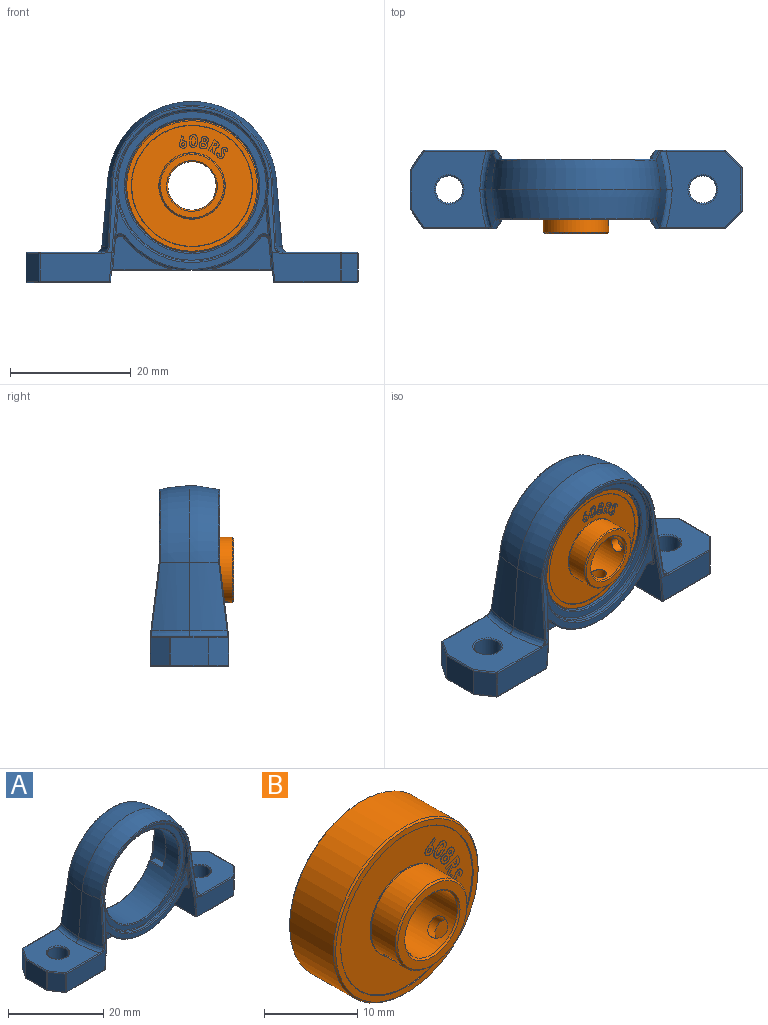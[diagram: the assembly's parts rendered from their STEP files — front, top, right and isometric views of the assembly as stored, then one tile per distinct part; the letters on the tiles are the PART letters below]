
ASSEMBLY  parts=2 mates=1
PART A: 247 faces, bbox 55.2x14x30.2 mm
  f0: plane 22.96x7.55mm, normal (0,1,0), area 35.1mm2, adj f36,f150,f153,f155
  f1: plane 13.6x12.6mm, normal (0,0,-1), area 145.8mm2, adj f133,f134,f135,f136,f137,f138,f139
  f2: plane 12.6x12.38mm, normal (0,0,1), area 122.3mm2, adj f57,f58,f118,f119,f120,f121,f122,f147
  f3: plane 11.31x4.79mm, normal (0,1,0), area 51.3mm2, adj f124,f125,f145,f196,f202,f233
  f4: plane 11.9x4.79mm, normal (0,1,0), area 54mm2, adj f117,f118,f135,f195,f199,f230
  f5: plane 13.6x12.6mm, normal (0,0,-1), area 145.2mm2, adj f140,f141,f142,f143,f144,f145,f146
  f6: plane 7.18x4.6mm, normal (1,0,0), area 33mm2, adj f127,f141,f236,f239
  f7: plane 12.6x12.38mm, normal (0,0,1), area 121.7mm2, adj f55,f56,f125,f126,f127,f128,f129,f148
  f8: plane 6.22x4.6mm, normal (-1,0,0), area 28.6mm2, adj f120,f138,f224,f227
  f9: plane 26.19x11.92mm, normal (0,1,0), area 17mm2, adj f209,f217,f218,f222
  f10: plane 12.19x1.74mm, normal (0,0.99,0.12), area 7.6mm2, adj f199,f200,f207,f208,f212,f217
  f11: plane 12.19x1.74mm, normal (0,0.99,0.12), area 7.6mm2, adj f201,f202,f210,f211,f215,f218,f219
  f12: cylinder r=14mm len=22.23mm, axis (0,-1,0), area 92.4mm2, adj f51,f53,f64,f65,f69,f70,f107
  f13: plane 13.76x12.77mm, normal (-1,0,-0.09), area 79.2mm2, adj f51,f52,f74,f78,f80,f81,f84,f94
  f14: plane 13.76x12.77mm, normal (1,0,-0.09), area 79.2mm2, adj f53,f54,f77,f79,f82,f85,f89,f100
  f15: plane 25.25x10.33mm, normal (0,1,0), area 37.6mm2, adj f105,f107,f109,f110,f113,f114
  f16: cylinder r=11mm len=22mm, axis (0,1,0), area 448.7mm2, adj f47,f50,f132,f149,f152,f153,f157,f160
  f17: plane 26.19x11.92mm, normal (0,-1,0), area 17mm2, adj f179,f187,f188,f192
  f18: plane 11.31x4.79mm, normal (0,-1,0), area 51.3mm2, adj f129,f130,f144,f165,f169,f242
  f19: plane 11.9x4.79mm, normal (0,-1,0), area 54mm2, adj f122,f123,f134,f166,f172,f245
  f20: plane 12.19x1.74mm, normal (0,-0.99,0.12), area 7.6mm2, adj f171,f172,f180,f181,f185,f188
  f21: plane 12.19x1.74mm, normal (0,-0.99,0.12), area 7.6mm2, adj f169,f170,f177,f178,f182,f186,f187
  f22: cylinder r=14mm len=22.23mm, axis (0,1,0), area 92.4mm2, adj f52,f54,f62,f63,f86,f92,f95
  f23: plane 25.25x10.33mm, normal (0,-1,0), area 37.6mm2, adj f93,f95,f97,f98,f101,f102
  f24: cylinder r=12.5mm len=25mm, axis (0,-1,0), area 48.8mm2, adj f96,f99,f101,f103,f104,f131,f178,f179
  f25: plane 24.6x24.6mm, normal (0,-1,0), area 81.2mm2, adj f131,f132
  f26: plane 26.31x1.6mm, normal (0,0,-1), area 42.1mm2, adj f59,f60,f67,f68,f75,f76,f81,f82
  f27: plane 9.77x5.48mm, normal (0,-1,0), area 24mm2, adj f88,f89,f91,f92
  f28: plane 9.77x5.48mm, normal (0,-1,0), area 24mm2, adj f80,f83,f86,f87
  f29: cylinder r=25.08mm len=11.46mm, axis (-0.09,0,-1), area 63.8mm2, adj f31,f40,f57,f185,f189
  f30: cylinder r=25.08mm len=11.4mm, axis (-0.09,0,1), area 63.5mm2, adj f31,f41,f55,f182
  f31: revolved ~27.89x12.9mm, area 199.8mm2, adj f29,f30,f42,f186,f190,f191,f192
  f32: cylinder r=2.25mm len=4.6mm, axis (0,0,1), area 65mm2, adj f139,f147
  f33: plane 4.6x3.19mm, normal (-0.83,-0.55,0), area 17.6mm2, adj f121,f136,f224,f245
  f34: plane 4.6x2.71mm, normal (0.71,-0.71,0), area 17.6mm2, adj f128,f142,f239,f242
  f35: cylinder r=2.25mm len=4.6mm, axis (0,0,1), area 65mm2, adj f140,f148
  f36: cylinder r=12.5mm len=25mm, axis (0,1,0), area 142.5mm2, adj f0,f37,f45,f46,f47,f48,f49,f50
  f37: plane 22.96x7.55mm, normal (0,1,0), area 35.1mm2, adj f36,f156,f159,f160
  f38: plane 9.77x5.48mm, normal (0,1,0), area 24mm2, adj f70,f73,f76,f77
  f39: plane 9.77x5.48mm, normal (0,1,0), area 24mm2, adj f69,f71,f74,f75
  f40: cylinder r=25.09mm len=11.46mm, axis (-0.09,0,-1), area 63.8mm2, adj f29,f42,f58,f212,f216
  f41: cylinder r=25.09mm len=11.4mm, axis (-0.09,0,1), area 63.5mm2, adj f30,f42,f56,f215
  f42: revolved ~27.89x12.9mm, area 199.8mm2, adj f31,f40,f41,f219,f220,f221,f222
  f43: plane 4.6x3.19mm, normal (-0.83,0.55,0), area 17.6mm2, adj f119,f137,f227,f230
  f44: plane 4.6x2.71mm, normal (0.71,0.71,0), area 17.6mm2, adj f126,f143,f233,f236
  f45: plane 3.8x1.52mm, normal (0,0,-1), area 5.8mm2, adj f36,f47,f152,f155
  f46: plane 3.8x1.52mm, normal (0,0,1), area 5.8mm2, adj f36,f47,f159,f162
  f47: plane 9.72x2.63mm, normal (0,1,0), area 14.7mm2, adj f16,f36,f45,f46,f152,f162
  f48: plane 3.8x1.52mm, normal (0,0,-1), area 5.8mm2, adj f36,f50,f149,f150
  f49: plane 3.8x1.52mm, normal (0,0,1), area 5.8mm2, adj f36,f50,f156,f157
  f50: plane 9.72x2.63mm, normal (0,1,0), area 14.7mm2, adj f16,f36,f48,f49,f149,f157
  f51: cylinder r=1mm len=3.6mm, axis (0,-1,0), area 8.6mm2, adj f12,f13,f71,f110
  f52: cylinder r=1mm len=3.6mm, axis (0,1,0), area 8.6mm2, adj f13,f22,f83,f93
  f53: cylinder r=1mm len=3.6mm, axis (0,-1,0), area 8.6mm2, adj f12,f14,f73,f105
  f54: cylinder r=1mm len=3.6mm, axis (0,1,0), area 8.6mm2, adj f14,f22,f91,f98
  f55: bspline ~11.42x2.29mm, area 9.5mm2, adj f7,f30,f56,f130,f177
  f56: bspline ~7.28x2.2mm, area 9.5mm2, adj f7,f41,f55,f124,f211
  f57: bspline ~11.42x2.29mm, area 9.5mm2, adj f2,f29,f58,f123,f181
  f58: bspline ~8.05x2.18mm, area 9.5mm2, adj f2,f40,f57,f117,f207
  f59: bspline ~3.35x0.2mm, area 0.6mm2, adj f26,f60,f88,f90
  f60: bspline ~3.35x0.2mm, area 0.6mm2, adj f26,f59,f61,f87
  f61: bspline ~3.35x0.34mm, area 0.4mm2, adj f60,f62,f86,f87
  f62: bspline ~3.31x0.39mm, area 0.5mm2, adj f22,f61,f63,f86
  f63: bspline ~3.31x0.39mm, area 0.5mm2, adj f22,f62,f90,f92
  f64: bspline ~3.31x0.39mm, area 0.5mm2, adj f12,f65,f70,f72
  f65: bspline ~3.31x0.39mm, area 0.5mm2, adj f12,f64,f66,f69
  f66: bspline ~3.35x0.34mm, area 0.4mm2, adj f65,f67,f69,f75
  f67: bspline ~3.35x0.2mm, area 0.6mm2, adj f26,f66,f68,f75
  f68: bspline ~3.35x0.2mm, area 0.6mm2, adj f26,f67,f72,f76
  f69: torus R=14.2mm, axis (0,-1,0), area 3mm2, adj f12,f39,f65,f66,f71
  f70: torus R=14.2mm, axis (0,-1,0), area 3mm2, adj f12,f38,f64,f72,f73
  f71: torus R=0.8mm, axis (0,-1,0), area 0.7mm2, adj f39,f51,f69,f74
  f72: bspline ~3.35x0.34mm, area 0.4mm2, adj f64,f68,f70,f76
  f73: torus R=0.8mm, axis (0,-1,0), area 0.7mm2, adj f38,f53,f70,f77
  f74: cylinder r=0.2mm len=4.76mm, axis (0.09,0,-1), area 1.5mm2, adj f13,f39,f71,f78
  f75: cylinder r=0.2mm len=9.81mm, axis (1,0,0), area 3.1mm2, adj f26,f39,f66,f67,f78
  f76: cylinder r=0.2mm len=9.81mm, axis (1,0,0), area 3.1mm2, adj f26,f38,f68,f72,f79
  f77: cylinder r=0.2mm len=4.76mm, axis (-0.09,0,-1), area 1.5mm2, adj f14,f38,f73,f79
  f78: bspline ~0.4x0.4mm, area 0.1mm2, adj f13,f74,f75,f81
  f79: bspline ~0.47x0.47mm, area 0.1mm2, adj f14,f76,f77,f82
  f80: cylinder r=0.2mm len=4.76mm, axis (0.09,0,-1), area 1.5mm2, adj f13,f28,f83,f84
  f81: cylinder r=0.2mm len=1.6mm, axis (0,1,0), area 0.5mm2, adj f13,f26,f78,f84
  f82: cylinder r=0.2mm len=1.6mm, axis (0,-1,0), area 0.5mm2, adj f14,f26,f79,f85
  f83: torus R=0.8mm, axis (0,1,0), area 0.7mm2, adj f28,f52,f80,f86
  f84: bspline ~0.5x0.4mm, area 0.1mm2, adj f13,f80,f81,f87
  f85: bspline ~0.47x0.42mm, area 0.1mm2, adj f14,f82,f88,f89
  f86: torus R=14.2mm, axis (0,1,0), area 3mm2, adj f22,f28,f61,f62,f83
  f87: cylinder r=0.2mm len=9.81mm, axis (1,0,0), area 3.1mm2, adj f26,f28,f60,f61,f84
  f88: cylinder r=0.2mm len=9.81mm, axis (1,0,0), area 3.1mm2, adj f26,f27,f59,f85,f90
  f89: cylinder r=0.2mm len=4.76mm, axis (-0.09,0,-1), area 1.5mm2, adj f14,f27,f85,f91
  f90: bspline ~3.35x0.34mm, area 0.4mm2, adj f59,f63,f88,f92
  f91: torus R=0.8mm, axis (0,1,0), area 0.7mm2, adj f27,f54,f89,f92
  f92: torus R=14.2mm, axis (0,1,0), area 3mm2, adj f22,f27,f63,f90,f91
  f93: torus R=1.2mm, axis (0,-1,0), area 0.7mm2, adj f23,f52,f94,f95
  f94: bspline ~1.03x0.4mm, area 0.1mm2, adj f13,f93,f97
  f95: torus R=13.8mm, axis (0,-1,0), area 8mm2, adj f22,f23,f93,f98
  f96: cylinder r=0.2mm len=0.05mm, axis (0,-1,0), area 0mm2, adj f13,f24,f99,f174
  f97: cylinder r=0.2mm len=5.94mm, axis (-0.09,0,1), area 1.7mm2, adj f13,f23,f94,f99
  f98: torus R=1.2mm, axis (0,-1,0), area 0.7mm2, adj f23,f54,f95,f100
  f99: bspline ~1.39x0.42mm, area 0.3mm2, adj f24,f96,f97,f101
  f100: bspline ~1.03x0.4mm, area 0.1mm2, adj f14,f98,f102
  f101: torus R=12.7mm, axis (0,-1,0), area 10.2mm2, adj f23,f24,f99,f103
  f102: cylinder r=0.2mm len=5.94mm, axis (-0.09,0,-1), area 1.7mm2, adj f14,f23,f100,f103
  f103: bspline ~1.39x0.43mm, area 0.3mm2, adj f24,f101,f102,f104
  f104: cylinder r=0.2mm len=0.05mm, axis (0,-1,0), area 0mm2, adj f14,f24,f103,f175
  f105: torus R=1.2mm, axis (0,1,0), area 0.7mm2, adj f15,f53,f106,f107
  f106: bspline ~1.03x0.4mm, area 0.1mm2, adj f14,f105,f109
  f107: torus R=13.8mm, axis (0,1,0), area 8mm2, adj f12,f15,f105,f110
  f108: cylinder r=0.2mm len=0.05mm, axis (0,1,0), area 0mm2, adj f14,f36,f111,f204
  f109: cylinder r=0.2mm len=5.94mm, axis (-0.09,0,-1), area 1.7mm2, adj f14,f15,f106,f111
  f110: torus R=1.2mm, axis (0,1,0), area 0.7mm2, adj f15,f51,f107,f112
  f111: bspline ~1.39x0.42mm, area 0.3mm2, adj f36,f108,f109,f113
  f112: bspline ~1.03x0.4mm, area 0.1mm2, adj f13,f110,f114
  f113: torus R=12.7mm, axis (0,1,0), area 10.2mm2, adj f15,f36,f111,f115
  f114: cylinder r=0.2mm len=5.94mm, axis (-0.09,0,1), area 1.7mm2, adj f13,f15,f112,f115
  f115: bspline ~1.39x0.43mm, area 0.3mm2, adj f36,f113,f114,f116
  f116: cylinder r=0.2mm len=0.05mm, axis (0,1,0), area 0mm2, adj f13,f36,f115,f205
  f117: bspline ~1.15x0.47mm, area 0.2mm2, adj f4,f58,f118,f203
  f118: cylinder r=0.2mm len=10.25mm, axis (-1,0,0), area 3.2mm2, adj f2,f4,f117,f229
  f119: cylinder r=0.2mm len=3.3mm, axis (0.55,0.83,0), area 1.2mm2, adj f2,f43,f226,f229
  f120: cylinder r=0.2mm len=6.22mm, axis (0,1,0), area 2mm2, adj f2,f8,f223,f226
  f121: cylinder r=0.2mm len=3.3mm, axis (-0.55,0.83,0), area 1.2mm2, adj f2,f33,f223,f244
  f122: cylinder r=0.2mm len=10.25mm, axis (-1,0,0), area 3.2mm2, adj f2,f19,f123,f244
  f123: bspline ~1.15x0.47mm, area 0.2mm2, adj f19,f57,f122,f176
  f124: bspline ~1.15x0.47mm, area 0.2mm2, adj f3,f56,f125,f206
  f125: cylinder r=0.2mm len=9.67mm, axis (-1,0,0), area 3mm2, adj f3,f7,f124,f232
  f126: cylinder r=0.2mm len=2.85mm, axis (-0.71,0.71,0), area 1.2mm2, adj f7,f44,f232,f235
  f127: cylinder r=0.2mm len=7.18mm, axis (0,1,0), area 2.3mm2, adj f6,f7,f235,f238
  f128: cylinder r=0.2mm len=2.85mm, axis (0.71,0.71,0), area 1.2mm2, adj f7,f34,f238,f241
  f129: cylinder r=0.2mm len=9.67mm, axis (-1,0,0), area 3mm2, adj f7,f18,f130,f241
  f130: bspline ~1.15x0.47mm, area 0.2mm2, adj f18,f55,f129,f173
  f131: torus R=12.3mm, axis (0,-1,0), area 24.5mm2, adj f24,f25
  f132: torus R=11.2mm, axis (0,-1,0), area 21.9mm2, adj f16,f25
  f133: cylinder r=0.2mm len=12.6mm, axis (0,-1,0), area 3.7mm2, adj f1,f14,f164,f193
  f134: cylinder r=0.2mm len=11.48mm, axis (1,0,0), area 3.6mm2, adj f1,f19,f164,f246
  f135: cylinder r=0.2mm len=11.48mm, axis (1,0,0), area 3.6mm2, adj f1,f4,f193,f231
  f136: cylinder r=0.2mm len=3.3mm, axis (-0.55,0.83,0), area 1.2mm2, adj f1,f33,f225,f246
  f137: cylinder r=0.2mm len=3.3mm, axis (0.55,0.83,0), area 1.2mm2, adj f1,f43,f228,f231
  f138: cylinder r=0.2mm len=6.22mm, axis (0,1,0), area 2mm2, adj f1,f8,f225,f228
  f139: torus R=2.45mm, axis (0,0,1), area 4.6mm2, adj f1,f32
  f140: torus R=2.45mm, axis (0,0,-1), area 4.6mm2, adj f5,f35
  f141: cylinder r=0.2mm len=7.18mm, axis (0,1,0), area 2.3mm2, adj f5,f6,f237,f240
  f142: cylinder r=0.2mm len=2.85mm, axis (0.71,0.71,0), area 1.2mm2, adj f5,f34,f240,f243
  f143: cylinder r=0.2mm len=2.85mm, axis (-0.71,0.71,0), area 1.2mm2, adj f5,f44,f234,f237
  f144: cylinder r=0.2mm len=10.89mm, axis (1,0,0), area 3.4mm2, adj f5,f18,f163,f243
  f145: cylinder r=0.2mm len=10.89mm, axis (1,0,0), area 3.4mm2, adj f3,f5,f194,f234
  f146: cylinder r=0.2mm len=12.6mm, axis (0,-1,0), area 3.7mm2, adj f5,f13,f163,f194
  f147: torus R=2.45mm, axis (0,0,-1), area 4.6mm2, adj f2,f32
  f148: torus R=2.45mm, axis (0,0,1), area 4.6mm2, adj f7,f35
  f149: cylinder r=0.2mm len=3.8mm, axis (0,1,0), area 0.8mm2, adj f16,f48,f50,f151
  f150: cylinder r=0.2mm len=1.52mm, axis (-1,0,0), area 0.5mm2, adj f0,f36,f48,f151
  f151: sphere r=0.2mm, area 0mm2, adj f149,f150,f153
  f152: cylinder r=0.2mm len=3.8mm, axis (0,1,0), area 0.8mm2, adj f16,f45,f47,f154
  f153: torus R=11.2mm, axis (0,1,0), area 7.7mm2, adj f0,f16,f151,f154
  f154: sphere r=0.2mm, area 0mm2, adj f152,f153,f155
  f155: cylinder r=0.2mm len=1.52mm, axis (-1,0,0), area 0.5mm2, adj f0,f36,f45,f154
  f156: cylinder r=0.2mm len=1.52mm, axis (1,0,0), area 0.5mm2, adj f36,f37,f49,f158
  f157: cylinder r=0.2mm len=3.8mm, axis (0,1,0), area 0.8mm2, adj f16,f49,f50,f158
  f158: sphere r=0.2mm, area 0mm2, adj f156,f157,f160
  f159: cylinder r=0.2mm len=1.52mm, axis (1,0,0), area 0.5mm2, adj f36,f37,f46,f161
  f160: torus R=11.2mm, axis (0,1,0), area 7.7mm2, adj f16,f37,f158,f161
  f161: sphere r=0.2mm, area 0mm2, adj f159,f160,f162
  f162: cylinder r=0.2mm len=3.8mm, axis (0,1,0), area 0.8mm2, adj f16,f46,f47,f161
  f163: sphere r=0.2mm, area 0.1mm2, adj f144,f146,f165
  f164: sphere r=0.2mm, area 0.1mm2, adj f133,f134,f166
  f165: cylinder r=0.2mm len=4.81mm, axis (0.09,0,-1), area 1.5mm2, adj f13,f18,f163,f167
  f166: cylinder r=0.2mm len=4.81mm, axis (0.09,0,1), area 1.5mm2, adj f14,f19,f164,f168
  f167: sphere r=0.2mm, area 0mm2, adj f165,f169,f170
  f168: sphere r=0.2mm, area 0mm2, adj f166,f171,f172
  f169: cylinder r=0.2mm len=0.97mm, axis (-1,0,0), area 0mm2, adj f18,f21,f167,f173
  f170: cylinder r=0.2mm len=8.84mm, axis (-0.09,0.12,0.99), area 2.8mm2, adj f13,f21,f167,f174
  f171: cylinder r=0.2mm len=8.84mm, axis (-0.09,-0.12,-0.99), area 2.8mm2, adj f14,f20,f168,f175
  f172: cylinder r=0.2mm len=0.97mm, axis (1,0,0), area 0mm2, adj f19,f20,f168,f176
  f173: sphere r=0.2mm, area 0mm2, adj f130,f169,f177
  f174: sphere r=0.2mm, area 0mm2, adj f96,f170,f178
  f175: sphere r=0.2mm, area 0mm2, adj f104,f171,f180
  f176: sphere r=0.2mm, area 0mm2, adj f123,f172,f181
  f177: bspline ~1.15x0.73mm, area 0.3mm2, adj f21,f55,f173,f182
  f178: bspline ~3.39x0.62mm, area 1.1mm2, adj f21,f24,f174,f183
  f179: torus R=12.7mm, axis (0,-1,0), area 11.6mm2, adj f17,f24,f183,f184
  f180: bspline ~3.39x0.62mm, area 1.1mm2, adj f20,f24,f175,f184
  f181: bspline ~1.13x0.79mm, area 0.3mm2, adj f20,f57,f176,f185
  f182: bspline ~13.27x1.78mm, area 2.9mm2, adj f21,f30,f177,f186
  f183: bspline ~0.22x0.22mm, area 0mm2, adj f24,f178,f179,f187
  f184: bspline ~0.22x0.21mm, area 0mm2, adj f24,f179,f180,f188
  f185: bspline ~13.27x1.78mm, area 3mm2, adj f20,f29,f181,f189
  f186: bspline ~3.79x0.63mm, area 0mm2, adj f21,f31,f182,f190
  f187: cylinder r=0.2mm len=0.45mm, axis (1,0,0), area 0mm2, adj f17,f21,f183,f190
  f188: cylinder r=0.2mm len=0.45mm, axis (1,0,0), area 0mm2, adj f17,f20,f184,f189,f191
  f189: bspline ~0.2x0.16mm, area 0mm2, adj f29,f185,f188,f191
  f190: bspline ~0.21x0.17mm, area 0mm2, adj f31,f186,f187,f192
  f191: bspline ~0.21x0.18mm, area 0mm2, adj f31,f188,f189,f192
  f192: bspline ~26.56x12.1mm, area 10.5mm2, adj f17,f31,f190,f191
  f193: sphere r=0.2mm, area 0mm2, adj f133,f135,f195
  f194: sphere r=0.2mm, area 0.1mm2, adj f145,f146,f196
  f195: cylinder r=0.2mm len=4.81mm, axis (0.09,0,1), area 1.5mm2, adj f4,f14,f193,f197
  f196: cylinder r=0.2mm len=4.81mm, axis (0.09,0,-1), area 1.5mm2, adj f3,f13,f194,f198
  f197: sphere r=0.2mm, area 0mm2, adj f195,f199,f200
  f198: sphere r=0.2mm, area 0mm2, adj f196,f201,f202
  f199: cylinder r=0.2mm len=0.97mm, axis (1,0,0), area 0mm2, adj f4,f10,f197,f203
  f200: cylinder r=0.2mm len=8.84mm, axis (-0.09,0.12,-0.99), area 2.8mm2, adj f10,f14,f197,f204
  f201: cylinder r=0.2mm len=8.84mm, axis (-0.09,-0.12,0.99), area 2.8mm2, adj f11,f13,f198,f205
  f202: cylinder r=0.2mm len=0.97mm, axis (-1,0,0), area 0mm2, adj f3,f11,f198,f206
  f203: sphere r=0.2mm, area 0mm2, adj f117,f199,f207
  f204: sphere r=0.2mm, area 0mm2, adj f108,f200,f208
  f205: sphere r=0.2mm, area 0mm2, adj f116,f201,f210
  f206: sphere r=0.2mm, area 0mm2, adj f124,f202,f211
  f207: bspline ~1.15x0.73mm, area 0.3mm2, adj f10,f58,f203,f212
  f208: bspline ~3.39x0.62mm, area 1.1mm2, adj f10,f36,f204,f213
  f209: torus R=12.7mm, axis (0,1,0), area 11.6mm2, adj f9,f36,f213,f214
  f210: bspline ~3.39x0.62mm, area 1.1mm2, adj f11,f36,f205,f214
  f211: bspline ~1.13x0.79mm, area 0.3mm2, adj f11,f56,f206,f215
  f212: bspline ~13.27x1.78mm, area 3mm2, adj f10,f40,f207,f216
  f213: bspline ~0.22x0.22mm, area 0mm2, adj f36,f208,f209,f217
  f214: bspline ~0.22x0.21mm, area 0mm2, adj f36,f209,f210,f218
  f215: bspline ~11.2x1.53mm, area 2.9mm2, adj f11,f41,f211,f219
  f216: bspline ~0.2x0.16mm, area 0mm2, adj f40,f212,f217,f220
  f217: cylinder r=0.2mm len=0.45mm, axis (-1,0,0), area 0mm2, adj f9,f10,f213,f216,f220
  f218: cylinder r=0.2mm len=0.45mm, axis (-1,0,0), area 0mm2, adj f9,f11,f214,f221
  f219: bspline ~3.79x0.63mm, area 0mm2, adj f11,f42,f215,f221
  f220: bspline ~0.21x0.18mm, area 0mm2, adj f42,f216,f217,f222
  f221: bspline ~0.2x0.17mm, area 0mm2, adj f42,f218,f219,f222
  f222: bspline ~26.66x12.66mm, area 10.5mm2, adj f9,f42,f220,f221
  f223: sphere r=0.2mm, area 0mm2, adj f120,f121,f224
  f224: cylinder r=0.2mm len=4.6mm, axis (0,0,1), area 0.5mm2, adj f8,f33,f223,f225
  f225: sphere r=0.2mm, area 0mm2, adj f136,f138,f224
  f226: sphere r=0.2mm, area 0mm2, adj f119,f120,f227
  f227: cylinder r=0.2mm len=4.6mm, axis (0,0,-1), area 0.5mm2, adj f8,f43,f226,f228
  f228: sphere r=0.2mm, area 0mm2, adj f137,f138,f227
  f229: sphere r=0.2mm, area 0mm2, adj f118,f119,f230
  f230: cylinder r=0.2mm len=4.6mm, axis (0,0,-1), area 0.9mm2, adj f4,f43,f229,f231
  f231: sphere r=0.2mm, area 0mm2, adj f135,f137,f230
  f232: sphere r=0.2mm, area 0mm2, adj f125,f126,f233
  f233: cylinder r=0.2mm len=4.6mm, axis (0,0,-1), area 0.7mm2, adj f3,f44,f232,f234
  f234: sphere r=0.2mm, area 0mm2, adj f143,f145,f233
  f235: sphere r=0.2mm, area 0mm2, adj f126,f127,f236
  f236: cylinder r=0.2mm len=4.6mm, axis (0,0,1), area 0.7mm2, adj f6,f44,f235,f237
  f237: sphere r=0.2mm, area 0mm2, adj f141,f143,f236
  f238: sphere r=0.2mm, area 0mm2, adj f127,f128,f239
  f239: cylinder r=0.2mm len=4.6mm, axis (0,0,-1), area 0.7mm2, adj f6,f34,f238,f240
  f240: sphere r=0.2mm, area 0mm2, adj f141,f142,f239
  f241: sphere r=0.2mm, area 0mm2, adj f128,f129,f242
  f242: cylinder r=0.2mm len=4.6mm, axis (0,0,1), area 0.7mm2, adj f18,f34,f241,f243
  f243: sphere r=0.2mm, area 0mm2, adj f142,f144,f242
  f244: sphere r=0.2mm, area 0mm2, adj f121,f122,f245
  f245: cylinder r=0.2mm len=4.6mm, axis (0,0,1), area 0.9mm2, adj f19,f33,f244,f246
  f246: sphere r=0.2mm, area 0mm2, adj f134,f136,f245
PART B: 180 faces, bbox 22x10.9x22 mm
  f0: plane 20x20mm, normal (0,-1,0), area 209.6mm2, adj f7,f8,f95,f96,f97,f98,f99,f100
  f1: plane 20x20mm, normal (0,1,0), area 209.6mm2, adj f9,f10,f17,f18,f19,f20,f21,f22
  f2: plane 10.9x10.9mm, normal (0,1,0), area 37.9mm2, adj f13,f173
  f3: plane 21.6x21.6mm, normal (0,-1,0), area 49.1mm2, adj f11,f177
  f4: plane 21.6x21.6mm, normal (0,1,0), area 49.1mm2, adj f12,f174
  f5: cylinder r=11mm len=22mm, axis (0,1,0), area 456.2mm2, adj f174,f177
  f6: cylinder r=4mm len=10.45mm, axis (0,1,0), area 252.7mm2, adj f173,f175,f178,f179
  f7: cylinder r=10mm len=20mm, axis (0,-1,0), area 3.1mm2, adj f0,f11
  f8: cylinder r=5.5mm len=11mm, axis (0,-1,0), area 1.7mm2, adj f0,f14
  f9: cylinder r=10mm len=20mm, axis (0,-1,0), area 3.1mm2, adj f1,f12
  f10: cylinder r=5.5mm len=11mm, axis (0,-1,0), area 1.7mm2, adj f1,f13
  f11: cone r=10mm half-angle=45deg, axis (0,-1,0), area 4.5mm2, adj f3,f7
  f12: cone r=10.05mm half-angle=45deg, axis (0,1,0), area 4.5mm2, adj f4,f9
  f13: cone r=5.5mm half-angle=45deg, axis (0,-1,0), area 2.4mm2, adj f2,f10
  f14: cone r=5.45mm half-angle=45deg, axis (0,1,0), area 2.4mm2, adj f8,f16
  f15: plane 10.5x10.5mm, normal (0,-1,0), area 31.2mm2, adj f175,f176
  f16: cylinder r=5.45mm len=10.9mm, axis (0,1,0), area 115.1mm2, adj f14,f176,f178,f179
  f17: extruded ~0.6x0.26mm, area 0mm2, adj f1,f18,f32,f33
  f18: extruded ~0.56x0.49mm, area 0mm2, adj f1,f17,f19,f33
  f19: extruded ~0.64x0.58mm, area 0mm2, adj f1,f18,f20,f33
  f20: extruded ~0.31x0.3mm, area 0mm2, adj f1,f19,f21,f33
  f21: extruded ~0.21x0.21mm, area 0mm2, adj f1,f20,f22,f33
  f22: extruded ~0.35x0.23mm, area 0mm2, adj f1,f21,f23,f33
  f23: plane 0.3x0.22mm, normal (-0.8,0,0.6), area 0mm2, adj f1,f22,f24,f33
  f24: extruded ~0.68x0.36mm, area 0mm2, adj f1,f23,f25,f33
  f25: extruded ~0.62x0.55mm, area 0mm2, adj f1,f24,f26,f33
  f26: extruded ~0.43x0.26mm, area 0mm2, adj f1,f25,f27,f33
  f27: cylinder r=4.68mm len=0.28mm, axis (0,-1,0), area 0mm2, adj f1,f26,f28,f33
  f28: extruded ~0.3x0.22mm, area 0mm2, adj f1,f27,f29,f33
  f29: cylinder r=0.16mm len=0.09mm, axis (0,1,0), area 0mm2, adj f1,f28,f30,f33
  f30: extruded ~0.15x0.15mm, area 0mm2, adj f1,f29,f31,f33
  f31: extruded ~0.32x0.17mm, area 0mm2, adj f1,f30,f32,f33
  f32: plane 0.28x0.25mm, normal (0.67,0,-0.74), area 0mm2, adj f1,f17,f31,f33
  f33: plane 2.08x1.26mm, normal (0,1,0), area 1.4mm2, adj f17,f18,f19,f20,f21,f22,f23,f24
  f34: plane 2.11x1.86mm, normal (0,1,0), area 1.7mm2, adj f35,f36,f37,f38,f39,f40,f41,f42
  f35: plane 1.88x0.66mm, normal (0.33,0,0.94), area 0.1mm2, adj f1,f34,f36,f44
  f36: plane 0.36x0.13mm, normal (0.94,0,-0.33), area 0mm2, adj f1,f34,f35,f37
  f37: plane 0.8x0.28mm, normal (-0.33,0,-0.94), area 0mm2, adj f1,f34,f36,f38
  f38: plane 0.05x0.03mm, normal (0.94,0,-0.33), area 0mm2, adj f1,f34,f37,f39
  f39: plane 0.7x0.65mm, normal (0.74,0,0.68), area 0mm2, adj f1,f34,f38,f40
  f40: plane 0.39x0.14mm, normal (0.94,0,-0.33), area 0mm2, adj f1,f34,f39,f41
  f41: plane 0.74x0.68mm, normal (-0.73,0,-0.68), area 0.1mm2, adj f1,f34,f40,f42
  f42: extruded ~0.62x0.22mm, area 0mm2, adj f1,f34,f41,f43
  f43: extruded ~0.93x0.39mm, area 0.1mm2, adj f1,f34,f42,f44
  f44: plane 0.38x0.13mm, normal (-0.94,0,0.33), area 0mm2, adj f1,f34,f35,f43
  f45: plane 0.38x0.13mm, normal (-0.33,0,-0.94), area 0mm2, adj f34,f46,f49,f50
  f46: plane 0.11x0.05mm, normal (-0.94,0,0.33), area 0mm2, adj f34,f45,f47,f50
  f47: extruded ~0.3x0.25mm, area 0mm2, adj f34,f46,f48,f50
  f48: extruded ~0.38x0.13mm, area 0mm2, adj f34,f47,f49,f50
  f49: plane 0.1x0.05mm, normal (0.94,0,-0.33), area 0mm2, adj f34,f45,f48,f50
  f50: plane 0.49x0.47mm, normal (0,1,0), area 0.2mm2, adj f45,f46,f47,f48,f49
  f51: plane 2x1.77mm, normal (0,1,0), area 1.8mm2, adj f52,f53,f54,f55,f56,f57,f58,f59
  f52: extruded ~0.44x0.08mm, area 0mm2, adj f1,f51,f53,f59
  f53: extruded ~0.8x0.25mm, area 0mm2, adj f1,f51,f52,f54
  f54: extruded ~0.79x0.29mm, area 0mm2, adj f1,f51,f53,f55
  f55: extruded ~0.37x0.24mm, area 0mm2, adj f1,f51,f54,f56
  f56: extruded ~0.58x0.1mm, area 0mm2, adj f1,f51,f55,f57
  f57: extruded ~0.91x0.28mm, area 0.1mm2, adj f1,f51,f56,f58
  f58: extruded ~0.88x0.34mm, area 0.1mm2, adj f1,f51,f57,f59
  f59: cylinder r=0.6mm len=0.52mm, axis (0,-1,0), area 0mm2, adj f1,f51,f52,f58
  f60: extruded ~0.31x0.1mm, area 0mm2, adj f51,f61,f63,f68
  f61: extruded ~0.3x0.1mm, area 0mm2, adj f51,f60,f62,f68
  f62: cylinder r=0.22mm len=0.31mm, axis (0,1,0), area 0mm2, adj f51,f61,f63,f68
  f63: extruded ~0.31x0.1mm, area 0mm2, adj f51,f60,f62,f68
  f64: extruded ~0.42x0.13mm, area 0mm2, adj f51,f65,f67,f69
  f65: extruded ~0.41x0.16mm, area 0mm2, adj f51,f64,f66,f69
  f66: extruded ~0.42x0.13mm, area 0mm2, adj f51,f65,f67,f69
  f67: extruded ~0.41x0.16mm, area 0mm2, adj f51,f64,f66,f69
  f68: plane 0.45x0.45mm, normal (0,1,0), area 0.2mm2, adj f60,f61,f62,f63
  f69: plane 0.62x0.6mm, normal (0,1,0), area 0.3mm2, adj f64,f65,f66,f67
  f70: plane 1.9x1.86mm, normal (0,1,0), area 1.7mm2, adj f71,f72,f73,f74,f75,f76,f77,f78
  f71: extruded ~0.57x0.18mm, area 0mm2, adj f1,f70,f72,f75
  f72: extruded ~0.67x0.47mm, area 0mm2, adj f1,f70,f71,f73
  f73: extruded ~1.23x0.41mm, area 0.1mm2, adj f1,f70,f72,f74
  f74: extruded ~1.22x0.47mm, area 0.1mm2, adj f1,f70,f73,f75
  f75: extruded ~1.25x0.41mm, area 0.1mm2, adj f1,f70,f71,f74
  f76: extruded ~0.72x0.32mm, area 0mm2, adj f70,f77,f80,f81
  f77: extruded ~0.72x0.37mm, area 0mm2, adj f70,f76,f78,f81
  f78: extruded ~0.71x0.3mm, area 0mm2, adj f70,f77,f79,f81
  f79: extruded ~0.25x0.06mm, area 0mm2, adj f70,f78,f80,f81
  f80: extruded ~0.45x0.34mm, area 0mm2, adj f70,f76,f79,f81
  f81: plane 1.14x1.1mm, normal (0,1,0), area 0.7mm2, adj f76,f77,f78,f79,f80
  f82: plane 1.88x1.58mm, normal (0,1,0), area 1.3mm2, adj f83,f84,f85,f86,f87,f88,f89,f90
  f83: plane 0.94x0.62mm, normal (0.55,0,0.83), area 0.1mm2, adj f1,f82,f84,f89
  f84: extruded ~0.37x0.33mm, area 0mm2, adj f1,f82,f83,f85
  f85: extruded ~0.84x0.32mm, area 0mm2, adj f1,f82,f84,f86
  f86: extruded ~0.84x0.32mm, area 0mm2, adj f1,f82,f85,f87
  f87: extruded ~0.85x0.31mm, area 0mm2, adj f1,f82,f86,f88
  f88: plane 0.63x0.42mm, normal (-0.55,0,-0.83), area 0mm2, adj f1,f82,f87,f89
  f89: plane 0.3x0.2mm, normal (-0.83,0,0.56), area 0mm2, adj f1,f82,f83,f88
  f90: extruded ~0.36x0.13mm, area 0mm2, adj f82,f91,f93,f94
  f91: extruded ~0.35x0.14mm, area 0mm2, adj f82,f90,f92,f94
  f92: extruded ~0.36x0.12mm, area 0mm2, adj f82,f91,f93,f94
  f93: extruded ~0.36x0.14mm, area 0mm2, adj f82,f90,f92,f94
  f94: plane 0.54x0.52mm, normal (0,1,0), area 0.2mm2, adj f90,f91,f92,f93
  f95: extruded ~0.6x0.26mm, area 0mm2, adj f0,f96,f110,f111
  f96: extruded ~0.56x0.49mm, area 0mm2, adj f0,f95,f97,f111
  f97: extruded ~0.64x0.58mm, area 0mm2, adj f0,f96,f98,f111
  f98: extruded ~0.31x0.3mm, area 0mm2, adj f0,f97,f99,f111
  f99: extruded ~0.21x0.21mm, area 0mm2, adj f0,f98,f100,f111
  f100: extruded ~0.35x0.23mm, area 0mm2, adj f0,f99,f101,f111
  f101: plane 0.3x0.22mm, normal (0.8,0,0.6), area 0mm2, adj f0,f100,f102,f111
  f102: extruded ~0.68x0.36mm, area 0mm2, adj f0,f101,f103,f111
  f103: extruded ~0.62x0.55mm, area 0mm2, adj f0,f102,f104,f111
  f104: extruded ~0.43x0.26mm, area 0mm2, adj f0,f103,f105,f111
  f105: cylinder r=4.68mm len=0.28mm, axis (0,1,0), area 0mm2, adj f0,f104,f106,f111
  f106: extruded ~0.3x0.22mm, area 0mm2, adj f0,f105,f107,f111
  f107: cylinder r=0.16mm len=0.09mm, axis (0,-1,0), area 0mm2, adj f0,f106,f108,f111
  f108: extruded ~0.15x0.15mm, area 0mm2, adj f0,f107,f109,f111
  f109: extruded ~0.32x0.17mm, area 0mm2, adj f0,f108,f110,f111
  f110: plane 0.28x0.25mm, normal (-0.67,0,-0.74), area 0mm2, adj f0,f95,f109,f111
  f111: plane 2.08x1.26mm, normal (0,-1,0), area 1.4mm2, adj f95,f96,f97,f98,f99,f100,f101,f102
  f112: plane 2.11x1.86mm, normal (0,-1,0), area 1.7mm2, adj f113,f114,f115,f116,f117,f118,f119,f120
  f113: plane 1.88x0.66mm, normal (-0.33,0,0.94), area 0.1mm2, adj f0,f112,f114,f122
  f114: plane 0.36x0.13mm, normal (-0.94,0,-0.33), area 0mm2, adj f0,f112,f113,f115
  f115: plane 0.8x0.28mm, normal (0.33,0,-0.94), area 0mm2, adj f0,f112,f114,f116
  f116: plane 0.05x0.03mm, normal (-0.94,0,-0.33), area 0mm2, adj f0,f112,f115,f117
  f117: plane 0.7x0.65mm, normal (-0.74,0,0.68), area 0mm2, adj f0,f112,f116,f118
  f118: plane 0.39x0.14mm, normal (-0.94,0,-0.33), area 0mm2, adj f0,f112,f117,f119
  f119: plane 0.74x0.68mm, normal (0.73,0,-0.68), area 0.1mm2, adj f0,f112,f118,f120
  f120: extruded ~0.62x0.22mm, area 0mm2, adj f0,f112,f119,f121
  f121: extruded ~0.93x0.39mm, area 0.1mm2, adj f0,f112,f120,f122
  f122: plane 0.38x0.13mm, normal (0.94,0,0.33), area 0mm2, adj f0,f112,f113,f121
  f123: plane 0.38x0.13mm, normal (0.33,0,-0.94), area 0mm2, adj f112,f124,f127,f128
  f124: plane 0.11x0.05mm, normal (0.94,0,0.33), area 0mm2, adj f112,f123,f125,f128
  f125: extruded ~0.3x0.25mm, area 0mm2, adj f112,f124,f126,f128
  f126: extruded ~0.38x0.13mm, area 0mm2, adj f112,f125,f127,f128
  f127: plane 0.1x0.05mm, normal (-0.94,0,-0.33), area 0mm2, adj f112,f123,f126,f128
  f128: plane 0.49x0.47mm, normal (0,-1,0), area 0.2mm2, adj f123,f124,f125,f126,f127
  f129: plane 2x1.77mm, normal (0,-1,0), area 1.8mm2, adj f130,f131,f132,f133,f134,f135,f136,f137
  f130: extruded ~0.44x0.08mm, area 0mm2, adj f0,f129,f131,f137
  f131: extruded ~0.8x0.25mm, area 0mm2, adj f0,f129,f130,f132
  f132: extruded ~0.79x0.29mm, area 0mm2, adj f0,f129,f131,f133
  f133: extruded ~0.37x0.24mm, area 0mm2, adj f0,f129,f132,f134
  f134: extruded ~0.58x0.1mm, area 0mm2, adj f0,f129,f133,f135
  f135: extruded ~0.91x0.28mm, area 0.1mm2, adj f0,f129,f134,f136
  f136: extruded ~0.88x0.34mm, area 0.1mm2, adj f0,f129,f135,f137
  f137: cylinder r=0.6mm len=0.52mm, axis (0,1,0), area 0mm2, adj f0,f129,f130,f136
  f138: extruded ~0.31x0.1mm, area 0mm2, adj f129,f139,f141,f147
  f139: extruded ~0.3x0.1mm, area 0mm2, adj f129,f138,f140,f147
  f140: cylinder r=0.22mm len=0.31mm, axis (0,-1,0), area 0mm2, adj f129,f139,f141,f147
  f141: extruded ~0.31x0.1mm, area 0mm2, adj f129,f138,f140,f147
  f142: extruded ~0.42x0.13mm, area 0mm2, adj f129,f143,f145,f146
  f143: extruded ~0.41x0.16mm, area 0mm2, adj f129,f142,f144,f146
  f144: extruded ~0.42x0.13mm, area 0mm2, adj f129,f143,f145,f146
  f145: extruded ~0.41x0.16mm, area 0mm2, adj f129,f142,f144,f146
  f146: plane 0.62x0.6mm, normal (0,-1,0), area 0.3mm2, adj f142,f143,f144,f145
  f147: plane 0.45x0.45mm, normal (0,-1,0), area 0.2mm2, adj f138,f139,f140,f141
  f148: plane 1.9x1.86mm, normal (0,-1,0), area 1.7mm2, adj f149,f150,f151,f152,f153,f154,f155,f156
  f149: extruded ~0.57x0.18mm, area 0mm2, adj f0,f148,f150,f153
  f150: extruded ~0.67x0.47mm, area 0mm2, adj f0,f148,f149,f151
  f151: extruded ~1.23x0.41mm, area 0.1mm2, adj f0,f148,f150,f152
  f152: extruded ~1.22x0.47mm, area 0.1mm2, adj f0,f148,f151,f153
  f153: extruded ~1.25x0.41mm, area 0.1mm2, adj f0,f148,f149,f152
  f154: extruded ~0.72x0.32mm, area 0mm2, adj f148,f155,f158,f159
  f155: extruded ~0.72x0.37mm, area 0mm2, adj f148,f154,f156,f159
  f156: extruded ~0.71x0.3mm, area 0mm2, adj f148,f155,f157,f159
  f157: extruded ~0.25x0.06mm, area 0mm2, adj f148,f156,f158,f159
  f158: extruded ~0.45x0.34mm, area 0mm2, adj f148,f154,f157,f159
  f159: plane 1.14x1.1mm, normal (0,-1,0), area 0.7mm2, adj f154,f155,f156,f157,f158
  f160: plane 1.88x1.58mm, normal (0,-1,0), area 1.3mm2, adj f161,f162,f163,f164,f165,f166,f167,f168
  f161: plane 0.94x0.62mm, normal (-0.55,0,0.83), area 0.1mm2, adj f0,f160,f162,f167
  f162: extruded ~0.37x0.33mm, area 0mm2, adj f0,f160,f161,f163
  f163: extruded ~0.84x0.32mm, area 0mm2, adj f0,f160,f162,f164
  f164: extruded ~0.84x0.32mm, area 0mm2, adj f0,f160,f163,f165
  f165: extruded ~0.85x0.31mm, area 0mm2, adj f0,f160,f164,f166
  f166: plane 0.63x0.42mm, normal (0.55,0,-0.83), area 0mm2, adj f0,f160,f165,f167
  f167: plane 0.3x0.2mm, normal (0.83,0,0.56), area 0mm2, adj f0,f160,f161,f166
  f168: extruded ~0.36x0.13mm, area 0mm2, adj f160,f169,f171,f172
  f169: extruded ~0.35x0.14mm, area 0mm2, adj f160,f168,f170,f172
  f170: extruded ~0.36x0.12mm, area 0mm2, adj f160,f169,f171,f172
  f171: extruded ~0.36x0.14mm, area 0mm2, adj f160,f168,f170,f172
  f172: plane 0.54x0.52mm, normal (0,-1,0), area 0.2mm2, adj f168,f169,f170,f171
  f173: cone r=4.2mm half-angle=45deg, axis (0,1,0), area 7.3mm2, adj f2,f6
  f174: cone r=11mm half-angle=45deg, axis (0,-1,0), area 19.4mm2, adj f4,f5
  f175: cone r=4mm half-angle=45deg, axis (0,-1,0), area 7.3mm2, adj f6,f15
  f176: cone r=5.25mm half-angle=45deg, axis (0,1,0), area 9.5mm2, adj f15,f16
  f177: cone r=10.8mm half-angle=45deg, axis (0,1,0), area 19.4mm2, adj f3,f5
  f178: cylinder r=1.25mm len=2.85mm, axis (0.72,0,-0.69), area 11.8mm2, adj f6,f16
  f179: cylinder r=1.25mm len=2.85mm, axis (-0.72,0,-0.69), area 11.8mm2, adj f6,f16
PLACE A t=(2.29,0,16)mm fixed
PLACE B rot(axis=(0,-1,0),41.3deg) t=(2.29,3.5,16)mm
MATE revolute B.f5 <-> A.f12  axis (0,1,0) through (2.29,0,16)mm
